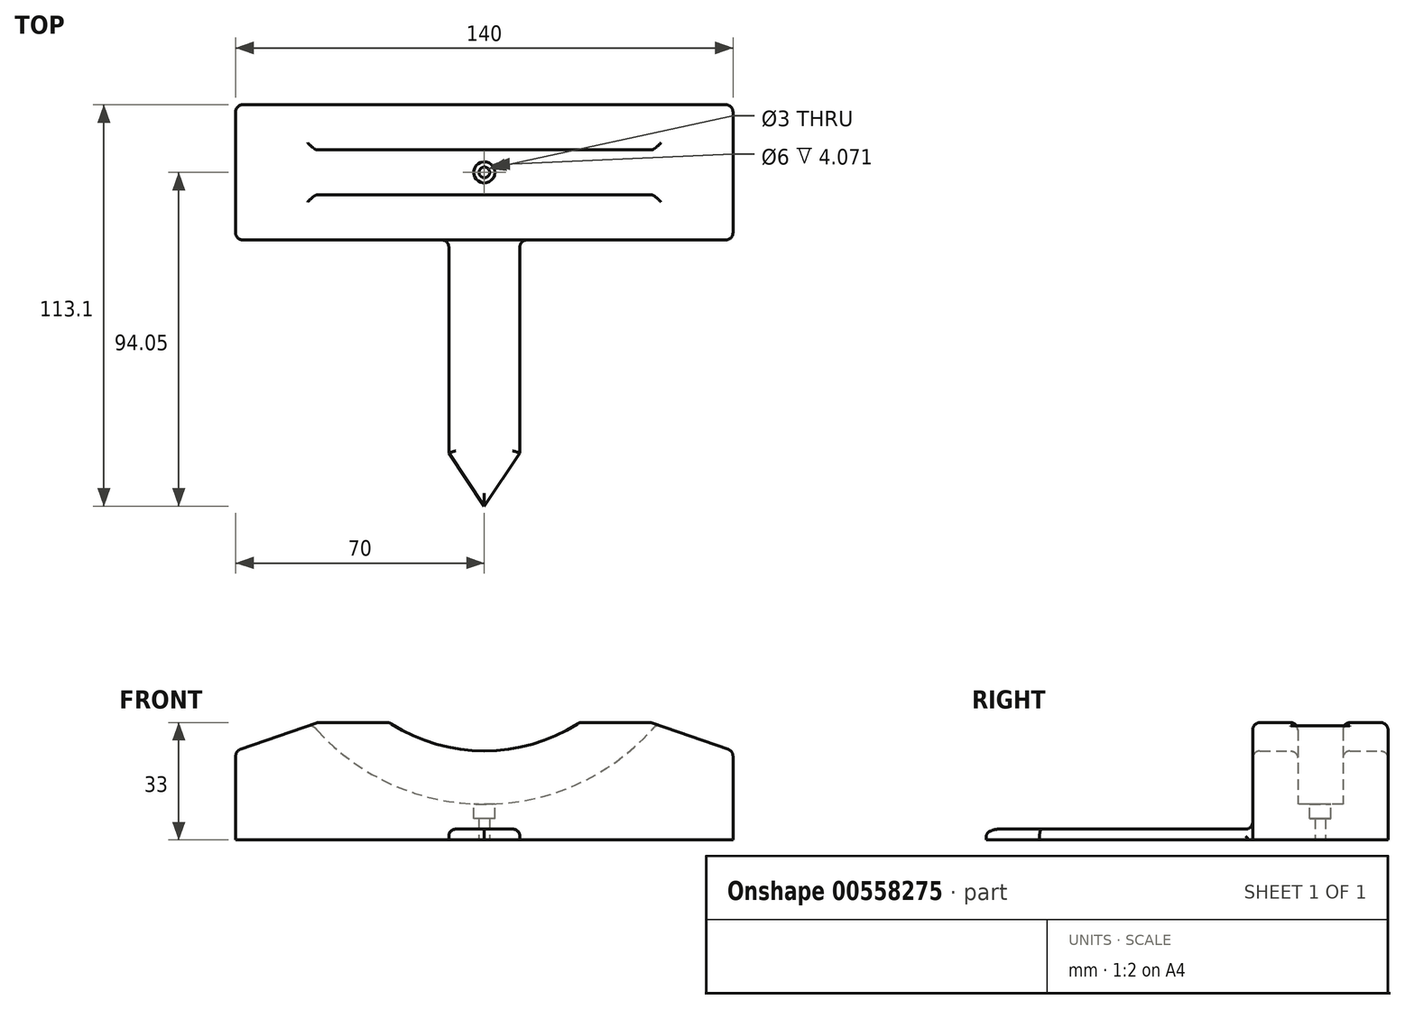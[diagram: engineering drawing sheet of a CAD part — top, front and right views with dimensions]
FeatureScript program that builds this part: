
annotation { "Feature Type Name" : "Feature", "Feature Type Description" : "" }
export const myFeature = defineFeature(function(context is Context, id is Id, definition is map)
    precondition{}
    {
        {
            var Q0;
            Q0=qCreatedBy(makeId("Front.planeOp"),FACE);
            var sketch = newSketch(context, id + "F0", { "sketchPlane" : qUnion([Q0])});
            skLineSegment(sketch, "E0.bottom", {"start": v(70, -13) * mm, "end": v(-70, -13) * mm});
            skLineSegment(sketch, "E0.top", {"start": v(47, 20) * mm, "end": v(26.68, 20) * mm});
            skLineSegment(sketch, "E0.left", {"start": v(70, -13) * mm, "end": v(70, 12) * mm});
            skLineSegment(sketch, "E0.right", {"start": v(-70, -13) * mm, "end": v(-70, 12) * mm});
            skPoint(sketch, "E0.middle", {"position": v(0, 0) * mm});
            skArc(sketch, "E1", {"start": v(-26.68, 20) * mm, "mid": v(0, 12) * mm, "end": v(26.68, 20) * mm});
            skLineSegment(sketch, "E2", {"start": v(-47, 20) * mm, "end": v(-70, 12) * mm});
            skLineSegment(sketch, "E3", {"start": v(70, 12) * mm, "end": v(47, 20) * mm});
            skLineSegment(sketch, "E4.trimOffspring", {"start": v(-26.68, 20) * mm, "end": v(-47, 20) * mm});
            skCircle(sketch, "E5", {"center": v(0, 60.5) * mm, "radius": 63.5 * mm, "construction": true});
            skSolve(sketch);
        }
        {
            var Q0;
            Q0 = qSketchRegion(id + "F0", true);
            extrude(context, id + "F1", {"entities" : qUnion([Q0]), "endBound" : BoundingType.SYMMETRIC, "depth" : 38.1 * mm, "offsetDistance" : 25 * mm});
        }
        {
            var Q0;
            Q0=qCreatedBy(makeId("Front.planeOp"),FACE);
            var sketch = newSketch(context, id + "F2", { "sketchPlane" : qUnion([Q0])});
            skCircle(sketch, "E6", {"center": v(0, 60.5) * mm, "radius": 63.5 * mm});
            skSolve(sketch);
        }
        {
            var Q0;
            Q0 = qSketchRegion(id + "F2", true);
            extrude(context, id + "F3", {"entities" : qUnion([Q0]), "operationType" : NewBodyOperationType.REMOVE, "endBound" : BoundingType.SYMMETRIC, "oppositeDirection" : true, "depth" : 12.7 * mm, "offsetDistance" : 25 * mm});
        }
        {
            var Q0;
            Q0=makeQuery(id+"F1.opExtrude","CAP_EDGE",EDGE,{"disambiguationData":[OSD([sQuery(id+"F0.wireOp",EDGE,"E0.right")])],"isStart":false});
            var Q1;
            Q1=makeQuery(id+"F1.opExtrude","CAP_EDGE",EDGE,{"disambiguationData":[OSD([sQuery(id+"F0.wireOp",EDGE,"E2")])],"isStart":false});
            var Q2;
            Q2=makeQuery(id+"F1.opExtrude","CAP_EDGE",EDGE,{"disambiguationData":[OSD([sQuery(id+"F0.wireOp",EDGE,"E4.trimOffspring")])],"isStart":false});
            var Q3;
            Q3=makeQuery(id+"F1.opExtrude","CAP_EDGE",EDGE,{"disambiguationData":[OSD([sQuery(id+"F0.wireOp",EDGE,"E1")])],"isStart":false});
            var Q4;
            Q4=makeQuery(id+"F1.opExtrude","CAP_EDGE",EDGE,{"disambiguationData":[OSD([sQuery(id+"F0.wireOp",EDGE,"E0.top")])],"isStart":false});
            var Q5;
            Q5=makeQuery(id+"F1.opExtrude","CAP_EDGE",EDGE,{"disambiguationData":[OSD([sQuery(id+"F0.wireOp",EDGE,"E3")])],"isStart":false});
            var Q6;
            Q6=makeQuery(id+"F1.opExtrude","CAP_EDGE",EDGE,{"disambiguationData":[OSD([sQuery(id+"F0.wireOp",EDGE,"E0.left")])],"isStart":false});
            var Q7;
            Q7=makeQuery(id+"F1.opExtrude","SWEPT_EDGE",EDGE,{"disambiguationData":[OSD([sQuery(id+"F0.wireOp",EDGE,"E0.left"),sQuery(id+"F0.wireOp",EDGE,"E3")])]});
            var Q8;
            {var subQ0=sQuery(id+"F0.wireOp",EDGE,"E3");var subQ1=sQuery(id+"F0.wireOp",EDGE,"E0.top");Q8=makeQuery(id+"F3.boolean.opBoolean","SPLIT",EDGE,{"disambiguationData":[TD([makeQuery(id+"F3.opExtrude","CAP_FACE",FACE,{"disambiguationData":[OSD([sQuery(id+"F2.wireOp",EDGE,"E6")])],"isStart":true})])],"derivedFrom":makeQuery(id+"F1.opExtrude","SWEPT_EDGE",EDGE,{"disambiguationData":[OSD([subQ1,subQ0])]})});}
            var Q9;
            {var subQ0=sQuery(id+"F0.wireOp",EDGE,"E1");var subQ1=sQuery(id+"F0.wireOp",EDGE,"E0.top");Q9=makeQuery(id+"F3.boolean.opBoolean","SPLIT",EDGE,{"disambiguationData":[TD([makeQuery(id+"F3.opExtrude","CAP_FACE",FACE,{"disambiguationData":[OSD([sQuery(id+"F2.wireOp",EDGE,"E6")])],"isStart":true})])],"derivedFrom":makeQuery(id+"F1.opExtrude","SWEPT_EDGE",EDGE,{"disambiguationData":[OSD([subQ1,subQ0])]})});}
            var Q10;
            {var subQ0=sQuery(id+"F0.wireOp",EDGE,"E1");var subQ1=sQuery(id+"F0.wireOp",EDGE,"E0.top");Q10=makeQuery(id+"F3.boolean.opBoolean","SPLIT",EDGE,{"disambiguationData":[TD([makeQuery(id+"F3.opExtrude","CAP_FACE",FACE,{"disambiguationData":[OSD([sQuery(id+"F2.wireOp",EDGE,"E6")])],"isStart":false})])],"derivedFrom":makeQuery(id+"F1.opExtrude","SWEPT_EDGE",EDGE,{"disambiguationData":[OSD([subQ1,subQ0])]})});}
            var Q11;
            Q11=makeQuery(id+"F1.opExtrude","SWEPT_FACE",FACE,{"disambiguationData":[OSD([sQuery(id+"F0.wireOp",EDGE,"E3")])]});
            var Q12;
            Q12=makeQuery(id+"F1.opExtrude","CAP_EDGE",EDGE,{"disambiguationData":[OSD([sQuery(id+"F0.wireOp",EDGE,"E0.left")])],"isStart":true});
            var Q13;
            {var subQ1=sQuery(id+"F0.wireOp",EDGE,"E1");Q13=makeQuery(id+"F3.boolean.opBoolean","SPLIT",FACE,{"disambiguationData":[TD([makeQuery(id+"F3.opExtrude","CAP_FACE",FACE,{"disambiguationData":[OSD([sQuery(id+"F2.wireOp",EDGE,"E6")])],"isStart":false})])],"derivedFrom":makeQuery(id+"F1.opExtrude","SWEPT_FACE",FACE,{"disambiguationData":[OSD([subQ1])]})});}
            var Q14;
            {var subQ1=sQuery(id+"F0.wireOp",EDGE,"E1");Q14=makeQuery(id+"F3.boolean.opBoolean","SPLIT",FACE,{"disambiguationData":[TD([makeQuery(id+"F3.opExtrude","CAP_FACE",FACE,{"disambiguationData":[OSD([sQuery(id+"F2.wireOp",EDGE,"E6")])],"isStart":true})])],"derivedFrom":makeQuery(id+"F1.opExtrude","SWEPT_FACE",FACE,{"disambiguationData":[OSD([subQ1])]})});}
            var Q15;
            {var subQ0=sQuery(id+"F0.wireOp",EDGE,"E4.trimOffspring");Q15=makeQuery(id+"F3.boolean.opBoolean","SPLIT",FACE,{"disambiguationData":[TD([makeQuery(id+"F3.opExtrude","CAP_FACE",FACE,{"disambiguationData":[OSD([sQuery(id+"F2.wireOp",EDGE,"E6")])],"isStart":true})])],"derivedFrom":makeQuery(id+"F1.opExtrude","SWEPT_FACE",FACE,{"disambiguationData":[OSD([subQ0])]})});}
            var Q16;
            {var subQ0=sQuery(id+"F0.wireOp",EDGE,"E4.trimOffspring");Q16=makeQuery(id+"F3.boolean.opBoolean","SPLIT",FACE,{"disambiguationData":[TD([makeQuery(id+"F3.opExtrude","CAP_FACE",FACE,{"disambiguationData":[OSD([sQuery(id+"F2.wireOp",EDGE,"E6")])],"isStart":false})])],"derivedFrom":makeQuery(id+"F1.opExtrude","SWEPT_FACE",FACE,{"disambiguationData":[OSD([subQ0])]})});}
            var Q17;
            Q17=makeQuery(id+"F1.opExtrude","SWEPT_FACE",FACE,{"disambiguationData":[OSD([sQuery(id+"F0.wireOp",EDGE,"E2")])]});
            var Q18;
            Q18=makeQuery(id+"F1.opExtrude","CAP_EDGE",EDGE,{"disambiguationData":[OSD([sQuery(id+"F0.wireOp",EDGE,"E0.right")])],"isStart":true});
            var Q19;
            {var subQ2=sQuery(id+"F0.wireOp",EDGE,"E0.top");Q19=makeQuery(id+"F3.boolean.opBoolean","SPLIT",FACE,{"disambiguationData":[TD([makeQuery(id+"F3.opExtrude","CAP_FACE",FACE,{"disambiguationData":[OSD([sQuery(id+"F2.wireOp",EDGE,"E6")])],"isStart":false})])],"derivedFrom":makeQuery(id+"F1.opExtrude","SWEPT_FACE",FACE,{"disambiguationData":[OSD([subQ2])]})});}
            var Q20;
            {var subQ2=sQuery(id+"F0.wireOp",EDGE,"E0.top");Q20=makeQuery(id+"F3.boolean.opBoolean","SPLIT",FACE,{"disambiguationData":[TD([makeQuery(id+"F3.opExtrude","CAP_FACE",FACE,{"disambiguationData":[OSD([sQuery(id+"F2.wireOp",EDGE,"E6")])],"isStart":true})])],"derivedFrom":makeQuery(id+"F1.opExtrude","SWEPT_FACE",FACE,{"disambiguationData":[OSD([subQ2])]})});}
            fillet(context, id + "F4", {"entities" : qUnion([Q0, Q1, Q2, Q3, Q4, Q5, Q6, Q7, Q8, Q9, Q10, Q11, Q12, Q13, Q14, Q15, Q16, Q17, Q18, Q19, Q20]), "radius" : 2 * mm, "tangentPropagation" : true, "allowEdgeOverflow" : false});
        }
        {
            var Q0;
            Q0=makeQuery(id+"F1.opExtrude","SWEPT_FACE",FACE,{"disambiguationData":[OSD([sQuery(id+"F0.wireOp",EDGE,"E0.bottom")])]});
            var sketch = newSketch(context, id + "F5", { "sketchPlane" : qUnion([Q0])});
            skCircle(sketch, "E7", {"center": v(0, 0) * mm, "radius": 1.5 * mm});
            skSolve(sketch);
        }
        {
            var Q0;
            Q0 = qSketchRegion(id + "F5", true);
            extrude(context, id + "F6", {"entities" : qUnion([Q0]), "operationType" : NewBodyOperationType.REMOVE, "endBound" : BoundingType.THROUGH_ALL, "oppositeDirection" : true, "depth" : 25 * mm, "offsetDistance" : 25 * mm});
        }
        {
            var Q0;
            Q0=qCreatedBy(makeId("Top.planeOp"),FACE);
            var sketch = newSketch(context, id + "F7", { "sketchPlane" : qUnion([Q0])});
            skCircle(sketch, "E8", {"center": v(0, 0) * mm, "radius": 3 * mm});
            skSolve(sketch);
        }
        {
            var Q0;
            Q0 = qSketchRegion(id + "F7", true);
            extrude(context, id + "F8", {"entities" : qUnion([Q0]), "operationType" : NewBodyOperationType.REMOVE, "oppositeDirection" : true, "depth" : 7 * mm, "offsetDistance" : 25 * mm});
        }
        {
            var Q0;
            Q0=makeQuery(id+"F1.opExtrude","CAP_FACE",FACE,{"disambiguationData":[OSD([sQuery(id+"F0.wireOp",EDGE,"E0.bottom"),sQuery(id+"F0.wireOp",EDGE,"E0.top"),sQuery(id+"F0.wireOp",EDGE,"E0.left"),sQuery(id+"F0.wireOp",EDGE,"E0.right"),sQuery(id+"F0.wireOp",EDGE,"E1"),sQuery(id+"F0.wireOp",EDGE,"E2"),sQuery(id+"F0.wireOp",EDGE,"E3"),sQuery(id+"F0.wireOp",EDGE,"E4.trimOffspring")])],"isStart":false});
            var sketch = newSketch(context, id + "F9", { "sketchPlane" : qUnion([Q0])});
            skLineSegment(sketch, "E9.bottom", {"start": v(-10, -13) * mm, "end": v(10, -13) * mm});
            skLineSegment(sketch, "E9.top", {"start": v(-10, -10) * mm, "end": v(10, -10) * mm});
            skLineSegment(sketch, "E9.left", {"start": v(-10, -13) * mm, "end": v(-10, -10) * mm});
            skLineSegment(sketch, "E9.right", {"start": v(10, -13) * mm, "end": v(10, -10) * mm});
            skSolve(sketch);
        }
        {
            var Q0;
            Q0 = qSketchRegion(id + "F9", true);
            extrude(context, id + "F10", {"entities" : qUnion([Q0]), "operationType" : NewBodyOperationType.ADD, "depth" : 75 * mm, "offsetDistance" : 25 * mm});
        }
        {
            var Q0;
            Q0=makeQuery(id+"F10.opExtrude","SWEPT_FACE",FACE,{"disambiguationData":[OSD([sQuery(id+"F9.wireOp",EDGE,"E9.top")])]});
            var sketch = newSketch(context, id + "F11", { "sketchPlane" : qUnion([Q0])});
            skLineSegment(sketch, "E10", {"start": v(0, -94.05) * mm, "end": v(-10, -79.05) * mm});
            skLineSegment(sketch, "E11", {"start": v(-10, -79.05) * mm, "end": v(-10, -94.05) * mm});
            skLineSegment(sketch, "E12", {"start": v(-10, -94.05) * mm, "end": v(0, -94.05) * mm});
            skLineSegment(sketch, "E13", {"start": v(0, -94.05) * mm, "end": v(10, -79.05) * mm});
            skLineSegment(sketch, "E14", {"start": v(10, -79.05) * mm, "end": v(10, -94.05) * mm});
            skLineSegment(sketch, "E15", {"start": v(10, -94.05) * mm, "end": v(0, -94.05) * mm});
            skSolve(sketch);
        }
        {
            var Q0;
            Q0 = qSketchRegion(id + "F11", true);
            extrude(context, id + "F12", {"entities" : qUnion([Q0]), "operationType" : NewBodyOperationType.REMOVE, "endBound" : BoundingType.THROUGH_ALL, "oppositeDirection" : true, "depth" : 25 * mm, "offsetDistance" : 25 * mm});
        }
        {
            var Q0;
            Q0=makeQuery(id+"F10.opExtrude","SWEPT_FACE",FACE,{"disambiguationData":[OSD([sQuery(id+"F9.wireOp",EDGE,"E9.top")])]});
            fillet(context, id + "F13", {"entities" : qUnion([Q0]), "radius" : 2 * mm, "tangentPropagation" : true, "allowEdgeOverflow" : false});
        }
    });
